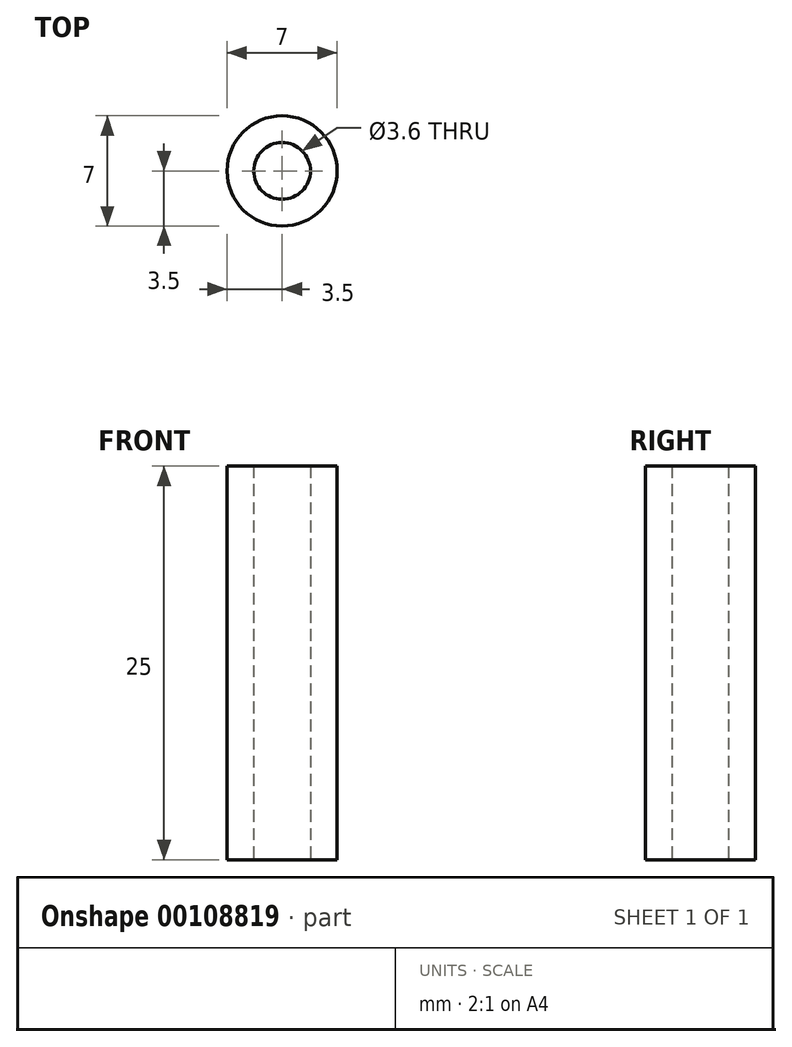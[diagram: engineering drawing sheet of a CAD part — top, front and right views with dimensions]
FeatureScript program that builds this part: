
annotation { "Feature Type Name" : "Feature", "Feature Type Description" : "" }
export const myFeature = defineFeature(function(context is Context, id is Id, definition is map)
    precondition{}
    {
        {
            var Q0;
            Q0=qCreatedBy(makeId("Top.planeOp"),FACE);
            var sketch = newSketch(context, id + "F0", { "sketchPlane" : qUnion([Q0])});
            skCircle(sketch, "E0", {"center": v(0, 0) * mm, "radius": 1.8 * mm});
            skCircle(sketch, "E1", {"center": v(0, 0) * mm, "radius": 3.5 * mm});
            skSolve(sketch);
        }
        {
            var Q0;
            Q0=makeQuery(id+"F0.imprint","IMPRINT",FACE,{"disambiguationData":[TD([[makeQuery(id+"F0.imprint","IMPRINT",EDGE,{"derivedFrom":sQuery(id+"F0.wireOp",EDGE,"E0")}),-1.0]])]});
            extrude(context, id + "F1", {"entities" : qUnion([Q0]), "depth" : 25 * mm, "offsetDistance" : 25 * mm});
        }
    });
